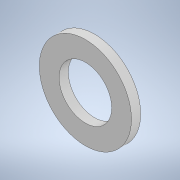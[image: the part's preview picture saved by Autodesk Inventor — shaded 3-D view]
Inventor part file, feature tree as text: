
AUTODESK INVENTOR PART (.ipt)
format: ipt  version: 2022 (Build 260153000, 153)  size: 103,424 bytes
history: native  units: mm
features: extrude x2, sketch x2
ambient origin geometry x8: Origin, YZ Plane, XZ Plane, XY Plane, X Axis, Y Axis, Z Axis, Center Point
bodies: Solid1 (feature_tree)
feature tree (4):
  extrude  "Extrusion1"  Depth=0.7mm TaperAngle=0.0deg
  extrude  "Extrusion2"  TaperAngle=0.0deg  [1 undecoded]
  sketch  "Sketch1"  dims[d0=7.0mm d1=0.7mm d2=0.0mm]
  sketch  "Sketch2"  dims[d3=4.0mm d4=0.0mm d5=0.0mm]
note: 1 required parameter value undecoded (feature->parameter linkage not recoverable at this tier; creation-order binding heuristic only, values carry confidence <= 0.55)
